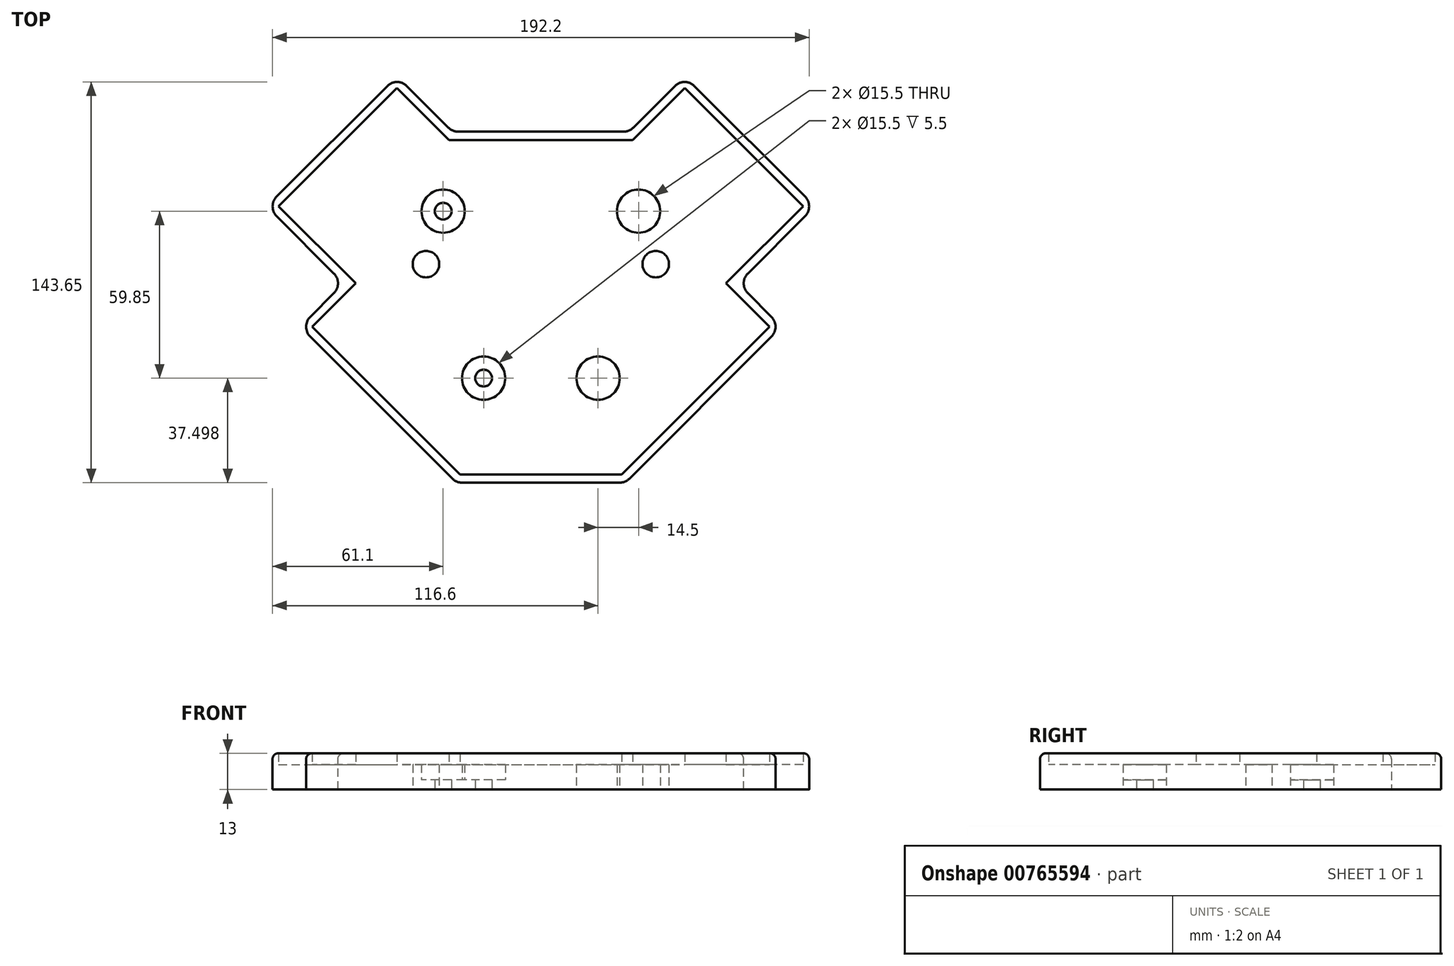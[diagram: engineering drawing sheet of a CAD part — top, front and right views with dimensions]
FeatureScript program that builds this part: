
annotation { "Feature Type Name" : "Feature", "Feature Type Description" : "" }
export const myFeature = defineFeature(function(context is Context, id is Id, definition is map)
    precondition{}
    {
        {
            var Q0;
            Q0=qCreatedBy(makeId("Top.planeOp"),FACE);
            var sketch = newSketch(context, id + "F0", { "sketchPlane" : qUnion([Q0])});
            skCircle(sketch, "E0", {"center": v(-35, 27.13) * mm, "radius": 7.75 * mm});
            skLineSegment(sketch, "E1", {"start": v(-35, 27.13) * mm, "end": v(0, 27.13) * mm, "construction": true});
            skLineSegment(sketch, "E2", {"start": v(0, 27.13) * mm, "end": v(0, 8.13) * mm, "construction": true});
            skLineSegment(sketch, "E3", {"start": v(0, 8.13) * mm, "end": v(-41.15, 8.13) * mm, "construction": true});
            skCircle(sketch, "E4", {"center": v(-41.15, 8.13) * mm, "radius": 4.75 * mm});
            skLineSegment(sketch, "E5", {"start": v(0, 27.13) * mm, "end": v(0, -32.72) * mm});
            skPoint(sketch, "E5.endSnap0", {"position": v(0, 17.63) * mm});
            skLineSegment(sketch, "E6", {"start": v(0, -32.72) * mm, "end": v(-20.5, -32.72) * mm, "construction": true});
            skCircle(sketch, "E7", {"center": v(-20.5, -32.72) * mm, "radius": 7.75 * mm});
            skCircle(sketch, "E8.MirrorC", {"center": v(20.5, -32.72) * mm, "radius": 7.75 * mm});
            skCircle(sketch, "E9.MirrorC", {"center": v(41.15, 8.13) * mm, "radius": 4.75 * mm});
            skCircle(sketch, "E10.MirrorC", {"center": v(35, 27.13) * mm, "radius": 7.75 * mm});
            skLineSegment(sketch, "E11", {"start": v(35, 27.13) * mm, "end": v(35, 55.63) * mm, "construction": true});
            skLineSegment(sketch, "E12", {"start": v(72.6, 55.63) * mm, "end": v(-68.52, 55.63) * mm, "construction": true});
            skLineSegment(sketch, "E13", {"start": v(20.5, -32.72) * mm, "end": v(20.5, -70.22) * mm, "construction": true});
            skLineSegment(sketch, "E14", {"start": v(74.92, -70.22) * mm, "end": v(-74.89, -70.22) * mm, "construction": true});
            skCircle(sketch, "E15", {"center": v(-35, 27.13) * mm, "radius": 3 * mm});
            skCircle(sketch, "E16", {"center": v(-20.5, -32.72) * mm, "radius": 3 * mm});
            skCircle(sketch, "E17.MirrorC", {"center": v(20.5, -32.72) * mm, "radius": 3 * mm});
            skCircle(sketch, "E18.MirrorC", {"center": v(35, 27.13) * mm, "radius": 3 * mm});
            skSolve(sketch);
        }
        {
            var Q0;
            Q0=qCreatedBy(makeId("Top.planeOp"),FACE);
            var sketch = newSketch(context, id + "F1", { "sketchPlane" : qUnion([Q0])});
            skLineSegment(sketch, "E19.bottom", {"start": v(-91.1, 28.83) * mm, "end": v(-51.5, 68.43) * mm});
            skLineSegment(sketch, "E19.top", {"start": v(-41.6, -20.66) * mm, "end": v(-2, 18.94) * mm});
            skLineSegment(sketch, "E19.left", {"start": v(-91.1, 28.83) * mm, "end": v(-41.6, -20.66) * mm});
            skLineSegment(sketch, "E19.right", {"start": v(-51.5, 68.43) * mm, "end": v(-2, 18.94) * mm});
            skLineSegment(sketch, "E20.MirrorCS", {"start": v(91.1, 28.83) * mm, "end": v(41.6, -20.66) * mm});
            skLineSegment(sketch, "E21.MirrorCS", {"start": v(91.1, 28.83) * mm, "end": v(51.5, 68.43) * mm});
            skLineSegment(sketch, "E22.MirrorCS", {"start": v(41.6, -20.66) * mm, "end": v(2, 18.94) * mm});
            skLineSegment(sketch, "E23.MirrorCS", {"start": v(51.5, 68.43) * mm, "end": v(2, 18.94) * mm});
            skLineSegment(sketch, "E24.bottom", {"start": v(-32, -16.72) * mm, "end": v(32, -16.72) * mm});
            skLineSegment(sketch, "E24.top", {"start": v(-32, -49.72) * mm, "end": v(32, -49.72) * mm});
            skLineSegment(sketch, "E24.left", {"start": v(-32, -16.72) * mm, "end": v(-32, -49.72) * mm});
            skLineSegment(sketch, "E24.right", {"start": v(32, -16.72) * mm, "end": v(32, -49.72) * mm});
            skLineSegment(sketch, "E25", {"start": v(-32, -49.72) * mm, "end": v(0, -49.72) * mm});
            skLineSegment(sketch, "E26", {"start": v(-25.2, -49.72) * mm, "end": v(-25.2, -65.22) * mm});
            skLineSegment(sketch, "E27", {"start": v(-25.2, -65.22) * mm, "end": v(14.8, -65.22) * mm});
            skLineSegment(sketch, "E28", {"start": v(14.8, -65.22) * mm, "end": v(14.8, -49.72) * mm});
            skLineSegment(sketch, "E29.bottom", {"start": v(65.64, -0.86) * mm, "end": v(47.96, -18.54) * mm});
            skLineSegment(sketch, "E29.top", {"start": v(79.07, -14.3) * mm, "end": v(61.4, -31.98) * mm});
            skLineSegment(sketch, "E29.left", {"start": v(65.64, -0.86) * mm, "end": v(79.07, -14.3) * mm});
            skLineSegment(sketch, "E29.right", {"start": v(47.96, -18.54) * mm, "end": v(61.4, -31.98) * mm});
            skLineSegment(sketch, "E30.MirrorCS", {"start": v(-79.07, -14.3) * mm, "end": v(-61.4, -31.98) * mm});
            skLineSegment(sketch, "E31.MirrorCS", {"start": v(-65.64, -0.86) * mm, "end": v(-79.07, -14.3) * mm});
            skLineSegment(sketch, "E32.MirrorCS", {"start": v(-65.64, -0.86) * mm, "end": v(-47.96, -18.54) * mm});
            skLineSegment(sketch, "E33.MirrorCS", {"start": v(-47.96, -18.54) * mm, "end": v(-61.4, -31.98) * mm});
            skSolve(sketch);
        }
        {
            var Q0;
            Q0=qCreatedBy(makeId("Top.planeOp"),FACE);
            var sketch = newSketch(context, id + "F2", { "sketchPlane" : qUnion([Q0])});
            skLineSegment(sketch, "E34", {"start": v(-31.62, 55.63) * mm, "end": v(0, 55.63) * mm});
            skPoint(sketch, "E35.visualSharp", {"position": v(-51.5, 75.5) * mm});
            skPoint(sketch, "E36.visualSharp", {"position": v(-98.17, 28.83) * mm});
            skLineSegment(sketch, "E37", {"start": v(-98.17, 28.83) * mm, "end": v(-51.5, 75.5) * mm});
            skLineSegment(sketch, "E38", {"start": v(0, 55.63) * mm, "end": v(-31.62, 55.63) * mm});
            skLineSegment(sketch, "E39", {"start": v(-31.62, 55.63) * mm, "end": v(-51.5, 75.5) * mm});
            skLineSegment(sketch, "E40", {"start": v(-98.17, 28.83) * mm, "end": v(-70.59, 1.26) * mm});
            skLineSegment(sketch, "E41", {"start": v(-70.59, 1.26) * mm, "end": v(-86.15, -14.3) * mm});
            skLineSegment(sketch, "E42", {"start": v(-86.15, -14.3) * mm, "end": v(-30.22, -70.22) * mm});
            skLineSegment(sketch, "E43", {"start": v(-30.22, -70.22) * mm, "end": v(0, -70.22) * mm});
            skLineSegment(sketch, "E44.MirrorCS", {"start": v(30.22, -70.22) * mm, "end": v(0, -70.22) * mm});
            skLineSegment(sketch, "E45.MirrorCS", {"start": v(86.15, -14.3) * mm, "end": v(30.22, -70.22) * mm});
            skLineSegment(sketch, "E46.MirrorCS", {"start": v(70.59, 1.26) * mm, "end": v(86.15, -14.3) * mm});
            skLineSegment(sketch, "E47.MirrorCS", {"start": v(98.17, 28.83) * mm, "end": v(70.59, 1.26) * mm});
            skLineSegment(sketch, "E48.MirrorCS", {"start": v(98.17, 28.83) * mm, "end": v(51.5, 75.5) * mm});
            skLineSegment(sketch, "E49.MirrorCS", {"start": v(0, 55.63) * mm, "end": v(31.62, 55.63) * mm});
            skLineSegment(sketch, "E50.MirrorCS", {"start": v(31.62, 55.63) * mm, "end": v(51.5, 75.5) * mm});
            skLineSegment(sketch, "E51.0", {"start": v(0, 52.63) * mm, "end": v(-32.86, 52.63) * mm});
            skLineSegment(sketch, "E51.1", {"start": v(-32.86, 52.63) * mm, "end": v(-51.5, 71.26) * mm});
            skLineSegment(sketch, "E51.2", {"start": v(-93.92, 28.83) * mm, "end": v(-51.5, 71.26) * mm});
            skLineSegment(sketch, "E51.3", {"start": v(66.35, 1.26) * mm, "end": v(81.9, -14.3) * mm});
            skLineSegment(sketch, "E51.4", {"start": v(93.92, 28.83) * mm, "end": v(66.35, 1.26) * mm});
            skLineSegment(sketch, "E51.5", {"start": v(93.92, 28.83) * mm, "end": v(51.5, 71.26) * mm});
            skLineSegment(sketch, "E51.6", {"start": v(32.86, 52.63) * mm, "end": v(51.5, 71.26) * mm});
            skLineSegment(sketch, "E51.7", {"start": v(81.9, -14.3) * mm, "end": v(28.98, -67.22) * mm});
            skLineSegment(sketch, "E51.8", {"start": v(28.98, -67.22) * mm, "end": v(0, -67.22) * mm});
            skLineSegment(sketch, "E51.9", {"start": v(-28.98, -67.22) * mm, "end": v(0, -67.22) * mm});
            skLineSegment(sketch, "E51.10", {"start": v(0, 52.63) * mm, "end": v(32.86, 52.63) * mm});
            skLineSegment(sketch, "E51.11", {"start": v(-81.9, -14.3) * mm, "end": v(-28.98, -67.22) * mm});
            skLineSegment(sketch, "E51.12", {"start": v(-66.35, 1.26) * mm, "end": v(-81.9, -14.3) * mm});
            skLineSegment(sketch, "E51.13", {"start": v(-93.92, 28.83) * mm, "end": v(-66.35, 1.26) * mm});
            skCircle(sketch, "E52.0", {"center": v(-35, 27.13) * mm, "radius": 3 * mm});
            skCircle(sketch, "E52.1", {"center": v(-35, 27.13) * mm, "radius": 7.75 * mm});
            skCircle(sketch, "E52.2", {"center": v(-41.15, 8.13) * mm, "radius": 4.75 * mm});
            skCircle(sketch, "E52.3", {"center": v(35, 27.13) * mm, "radius": 7.75 * mm});
            skCircle(sketch, "E52.4", {"center": v(35, 27.13) * mm, "radius": 3 * mm});
            skCircle(sketch, "E52.5", {"center": v(41.15, 8.13) * mm, "radius": 4.75 * mm});
            skCircle(sketch, "E52.6", {"center": v(20.5, -32.72) * mm, "radius": 7.75 * mm});
            skCircle(sketch, "E52.7", {"center": v(20.5, -32.72) * mm, "radius": 3 * mm});
            skCircle(sketch, "E52.8", {"center": v(-20.5, -32.72) * mm, "radius": 3 * mm});
            skCircle(sketch, "E52.9", {"center": v(-20.5, -32.72) * mm, "radius": 7.75 * mm});
            skSolve(sketch);
        }
        {
            var Q0;
            Q0=makeQuery(id+"F2.imprint","IMPRINT",FACE,{"disambiguationData":[TD([[makeQuery(id+"F2.imprint","IMPRINT",EDGE,{"derivedFrom":sQuery(id+"F2.wireOp",EDGE,"E51.0")}),1.0]])]});
            extrude(context, id + "F3", {"entities" : qUnion([Q0]), "flatOperationType" : FlatOperationType.REMOVE, "depth" : 9 * mm, "offsetDistance" : 25 * mm, "domain" : OperationDomain.MODEL});
        }
        {
            var Q0;
            Q0=makeQuery(id+"F2.imprint","IMPRINT",FACE,{"disambiguationData":[TD([[makeQuery(id+"F2.imprint","IMPRINT",EDGE,{"derivedFrom":sQuery(id+"F2.wireOp",EDGE,"E37")}),-1.0]])]});
            extrude(context, id + "F4", {"entities" : qUnion([Q0]), "operationType" : NewBodyOperationType.ADD, "flatOperationType" : FlatOperationType.REMOVE, "depth" : 13 * mm, "offsetDistance" : 25 * mm, "domain" : OperationDomain.MODEL});
        }
        {
            var Q0;
            Q0=makeQuery(id+"F0.imprint","IMPRINT",FACE,{"disambiguationData":[TD([[makeQuery(id+"F0.imprint","IMPRINT",EDGE,{"derivedFrom":sQuery(id+"F0.wireOp",EDGE,"E0")}),1.0]])]});
            var Q1;
            Q1=makeQuery(id+"F0.imprint","IMPRINT",FACE,{"disambiguationData":[TD([[makeQuery(id+"F0.imprint","IMPRINT",EDGE,{"derivedFrom":sQuery(id+"F0.wireOp",EDGE,"E10.MirrorC")}),-1.0]])]});
            var Q2;
            Q2=makeQuery(id+"F0.imprint","IMPRINT",FACE,{"disambiguationData":[TD([[makeQuery(id+"F0.imprint","IMPRINT",EDGE,{"derivedFrom":sQuery(id+"F0.wireOp",EDGE,"E8.MirrorC")}),-1.0]])]});
            var Q3;
            Q3=makeQuery(id+"F0.imprint","IMPRINT",FACE,{"disambiguationData":[TD([[makeQuery(id+"F0.imprint","IMPRINT",EDGE,{"derivedFrom":sQuery(id+"F0.wireOp",EDGE,"E7")}),1.0]])]});
            extrude(context, id + "F5", {"entities" : qUnion([Q0, Q1, Q2, Q3]), "operationType" : NewBodyOperationType.ADD, "flatOperationType" : FlatOperationType.REMOVE, "depth" : 3.5 * mm, "offsetDistance" : 25 * mm, "domain" : OperationDomain.MODEL});
        }
        {
            var Q0;
            Q0=makeQuery(id+"F4.opExtrude","SWEPT_EDGE",EDGE,{"disambiguationData":[OSD([sQuery(id+"F2.wireOp",EDGE,"E37"),sQuery(id+"F2.wireOp",EDGE,"E39")])]});
            var Q1;
            Q1=makeQuery(id+"F4.opExtrude","SWEPT_EDGE",EDGE,{"disambiguationData":[OSD([sQuery(id+"F2.wireOp",EDGE,"E38"),sQuery(id+"F2.wireOp",EDGE,"E39")])]});
            var Q2;
            Q2=makeQuery(id+"F4.opExtrude","SWEPT_EDGE",EDGE,{"disambiguationData":[OSD([sQuery(id+"F2.wireOp",EDGE,"E48.MirrorCS"),sQuery(id+"F2.wireOp",EDGE,"E50.MirrorCS")])]});
            var Q3;
            Q3=makeQuery(id+"F4.opExtrude","SWEPT_EDGE",EDGE,{"disambiguationData":[OSD([sQuery(id+"F2.wireOp",EDGE,"E47.MirrorCS"),sQuery(id+"F2.wireOp",EDGE,"E48.MirrorCS")])]});
            var Q4;
            Q4=makeQuery(id+"F4.opExtrude","SWEPT_EDGE",EDGE,{"disambiguationData":[OSD([sQuery(id+"F2.wireOp",EDGE,"E46.MirrorCS"),sQuery(id+"F2.wireOp",EDGE,"E47.MirrorCS")])]});
            var Q5;
            Q5=makeQuery(id+"F4.opExtrude","SWEPT_EDGE",EDGE,{"disambiguationData":[OSD([sQuery(id+"F2.wireOp",EDGE,"E45.MirrorCS"),sQuery(id+"F2.wireOp",EDGE,"E46.MirrorCS")])]});
            var Q6;
            Q6=makeQuery(id+"F4.opExtrude","SWEPT_EDGE",EDGE,{"disambiguationData":[OSD([sQuery(id+"F2.wireOp",EDGE,"E44.MirrorCS"),sQuery(id+"F2.wireOp",EDGE,"E45.MirrorCS")])]});
            var Q7;
            Q7=makeQuery(id+"F4.opExtrude","SWEPT_EDGE",EDGE,{"disambiguationData":[OSD([sQuery(id+"F2.wireOp",EDGE,"E42"),sQuery(id+"F2.wireOp",EDGE,"E43")])]});
            var Q8;
            Q8=makeQuery(id+"F4.opExtrude","SWEPT_EDGE",EDGE,{"disambiguationData":[OSD([sQuery(id+"F2.wireOp",EDGE,"E41"),sQuery(id+"F2.wireOp",EDGE,"E42")])]});
            var Q9;
            Q9=makeQuery(id+"F4.opExtrude","SWEPT_EDGE",EDGE,{"disambiguationData":[OSD([sQuery(id+"F2.wireOp",EDGE,"E40"),sQuery(id+"F2.wireOp",EDGE,"E41")])]});
            var Q10;
            Q10=makeQuery(id+"F4.opExtrude","SWEPT_EDGE",EDGE,{"disambiguationData":[OSD([sQuery(id+"F2.wireOp",EDGE,"E37"),sQuery(id+"F2.wireOp",EDGE,"E40")])]});
            var Q11;
            Q11=makeQuery(id+"F4.opExtrude","SWEPT_EDGE",EDGE,{"disambiguationData":[OSD([sQuery(id+"F2.wireOp",EDGE,"E49.MirrorCS"),sQuery(id+"F2.wireOp",EDGE,"E50.MirrorCS")])]});
            fillet(context, id + "F6", {"entities" : qUnion([Q0, Q1, Q2, Q3, Q4, Q5, Q6, Q7, Q8, Q9, Q10, Q11]), "radius" : 5 * mm, "tangentPropagation" : true, "defaultsChanged" : false, "vertexSettings" : [], "allowEdgeOverflow" : false});
        }
        {
            var Q0;
            Q0=makeQuery(id+"F4.opExtrude","CAP_EDGE",EDGE,{"disambiguationData":[OSD([sQuery(id+"F2.wireOp",EDGE,"E37")])],"isStart":false});
            var Q1;
            Q1=makeQuery(id+"F4.opExtrude","CAP_EDGE",EDGE,{"disambiguationData":[OSD([sQuery(id+"F2.wireOp",EDGE,"E39")])],"isStart":false});
            var Q2;
            Q2=makeQuery(id+"F4.opExtrude","CAP_EDGE",EDGE,{"disambiguationData":[OSD([sQuery(id+"F2.wireOp",EDGE,"E38"),sQuery(id+"F2.wireOp",EDGE,"E49.MirrorCS")])],"isStart":false});
            var Q3;
            Q3=makeQuery(id+"F4.opExtrude","CAP_EDGE",EDGE,{"disambiguationData":[OSD([sQuery(id+"F2.wireOp",EDGE,"E50.MirrorCS")])],"isStart":false});
            var Q4;
            Q4=makeQuery(id+"F4.opExtrude","CAP_EDGE",EDGE,{"disambiguationData":[OSD([sQuery(id+"F2.wireOp",EDGE,"E48.MirrorCS")])],"isStart":false});
            var Q5;
            Q5=makeQuery(id+"F4.opExtrude","CAP_EDGE",EDGE,{"disambiguationData":[OSD([sQuery(id+"F2.wireOp",EDGE,"E47.MirrorCS")])],"isStart":false});
            var Q6;
            Q6=makeQuery(id+"F4.opExtrude","CAP_EDGE",EDGE,{"disambiguationData":[OSD([sQuery(id+"F2.wireOp",EDGE,"E46.MirrorCS")])],"isStart":false});
            var Q7;
            Q7=makeQuery(id+"F4.opExtrude","CAP_EDGE",EDGE,{"disambiguationData":[OSD([sQuery(id+"F2.wireOp",EDGE,"E45.MirrorCS")])],"isStart":false});
            var Q8;
            Q8=makeQuery(id+"F4.opExtrude","CAP_EDGE",EDGE,{"disambiguationData":[OSD([sQuery(id+"F2.wireOp",EDGE,"E43"),sQuery(id+"F2.wireOp",EDGE,"E44.MirrorCS")])],"isStart":false});
            var Q9;
            Q9=makeQuery(id+"F4.opExtrude","CAP_EDGE",EDGE,{"disambiguationData":[OSD([sQuery(id+"F2.wireOp",EDGE,"E42")])],"isStart":false});
            var Q10;
            Q10=makeQuery(id+"F4.opExtrude","CAP_EDGE",EDGE,{"disambiguationData":[OSD([sQuery(id+"F2.wireOp",EDGE,"E41")])],"isStart":false});
            var Q11;
            Q11=makeQuery(id+"F4.opExtrude","CAP_EDGE",EDGE,{"disambiguationData":[OSD([sQuery(id+"F2.wireOp",EDGE,"E40")])],"isStart":false});
            fillet(context, id + "F7", {"entities" : qUnion([Q0, Q1, Q2, Q3, Q4, Q5, Q6, Q7, Q8, Q9, Q10, Q11]), "radius" : 2 * mm, "tangentPropagation" : true, "defaultsChanged" : false, "vertexSettings" : [], "allowEdgeOverflow" : false});
        }
    });
